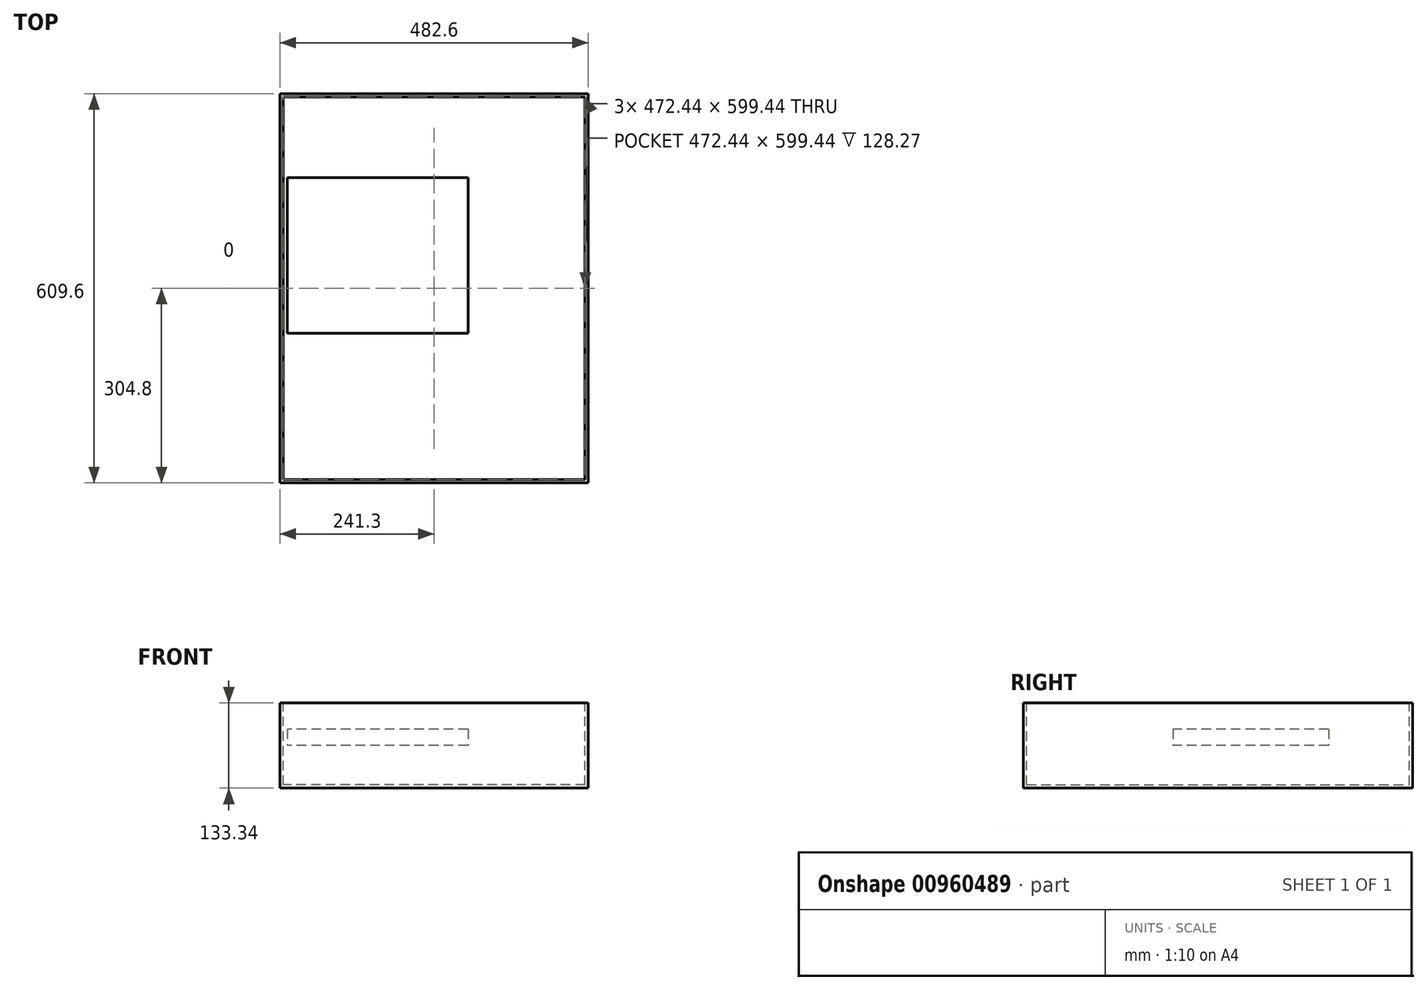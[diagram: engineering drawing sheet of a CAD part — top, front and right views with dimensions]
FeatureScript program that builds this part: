
annotation { "Feature Type Name" : "Feature", "Feature Type Description" : "" }
export const myFeature = defineFeature(function(context is Context, id is Id, definition is map)
    precondition{}
    {
        {
            var Q0;
            Q0=qCreatedBy(makeId("Front.planeOp"),FACE);
            var sketch = newSketch(context, id + "F0", { "sketchPlane" : qUnion([Q0])});
            skLineSegment(sketch, "E0.bottom", {"start": v(241.3, -66.67) * mm, "end": v(-241.3, -66.68) * mm});
            skLineSegment(sketch, "E0.top", {"start": v(241.3, 66.68) * mm, "end": v(-241.3, 66.67) * mm});
            skLineSegment(sketch, "E0.left", {"start": v(241.3, -66.67) * mm, "end": v(241.3, 66.68) * mm});
            skLineSegment(sketch, "E0.right", {"start": v(-241.3, -66.68) * mm, "end": v(-241.3, 66.67) * mm});
            skPoint(sketch, "E0.middle", {"position": v(0, 0) * mm});
            skSolve(sketch);
        }
        {
            var Q0;
            Q0=makeQuery(id+"F0.imprint","IMPRINT",FACE,{"disambiguationData":[TD([[makeQuery(id+"F0.imprint","IMPRINT",EDGE,{"derivedFrom":sQuery(id+"F0.wireOp",EDGE,"E0.bottom")}),-1.0]])]});
            var Q1;
            Q1=sQuery(id+"F0.wireOp",EDGE,"E0.right");
            var Q2;
            Q2=sQuery(id+"F0.wireOp",EDGE,"E0.bottom");
            var Q3;
            Q3=sQuery(id+"F0.wireOp",EDGE,"E0.left");
            var Q4;
            Q4=sQuery(id+"F0.wireOp",EDGE,"E0.top");
            extrude(context, id + "F1", {"entities" : qUnion([Q0]), "surfaceOperationType" : NewSurfaceOperationType.ADD, "surfaceEntities" : qUnion([Q1, Q2, Q3, Q4]), "depth" : 609.6 * mm, "offsetDistance" : 25.4 * mm});
        }
        {
            var Q0;
            Q0=qCreatedBy(makeId("Top.planeOp"),FACE);
            var sketch = newSketch(context, id + "F2", { "sketchPlane" : qUnion([Q0])});
            skLineSegment(sketch, "E1.bottom", {"start": v(52.93, -131.48) * mm, "end": v(-229.93, -131.48) * mm});
            skLineSegment(sketch, "E1.top", {"start": v(52.93, -375.32) * mm, "end": v(-229.93, -375.32) * mm});
            skLineSegment(sketch, "E1.left", {"start": v(52.93, -131.48) * mm, "end": v(52.93, -375.32) * mm});
            skPoint(sketch, "E1.middle", {"position": v(-99.47, -253.4) * mm});
            skLineSegment(sketch, "E2.0", {"start": v(-229.93, -131.48) * mm, "end": v(-229.93, -375.32) * mm});
            skPoint(sketch, "E1.right.end.orphan", {"position": v(-251.87, -375.32) * mm});
            skPoint(sketch, "E3.orphan", {"position": v(-251.87, -131.48) * mm});
            skSolve(sketch);
        }
        {
            var Q0;
            Q0 = qSketchRegion(id + "F2", true);
            extrude(context, id + "F3", {"entities" : qUnion([Q0]), "depth" : 25.4 * mm, "offsetDistance" : 25.4 * mm});
        }
        {
            var Q0;
            Q0=makeQuery(id+"F1.opExtrude","SWEPT_FACE",FACE,{"disambiguationData":[OSD([sQuery(id+"F0.wireOp",EDGE,"E0.top")])]});
            shell(context, id + "F4", {"entities" : qUnion([Q0]), "thickness" : 5.08 * mm});
        }
    });
